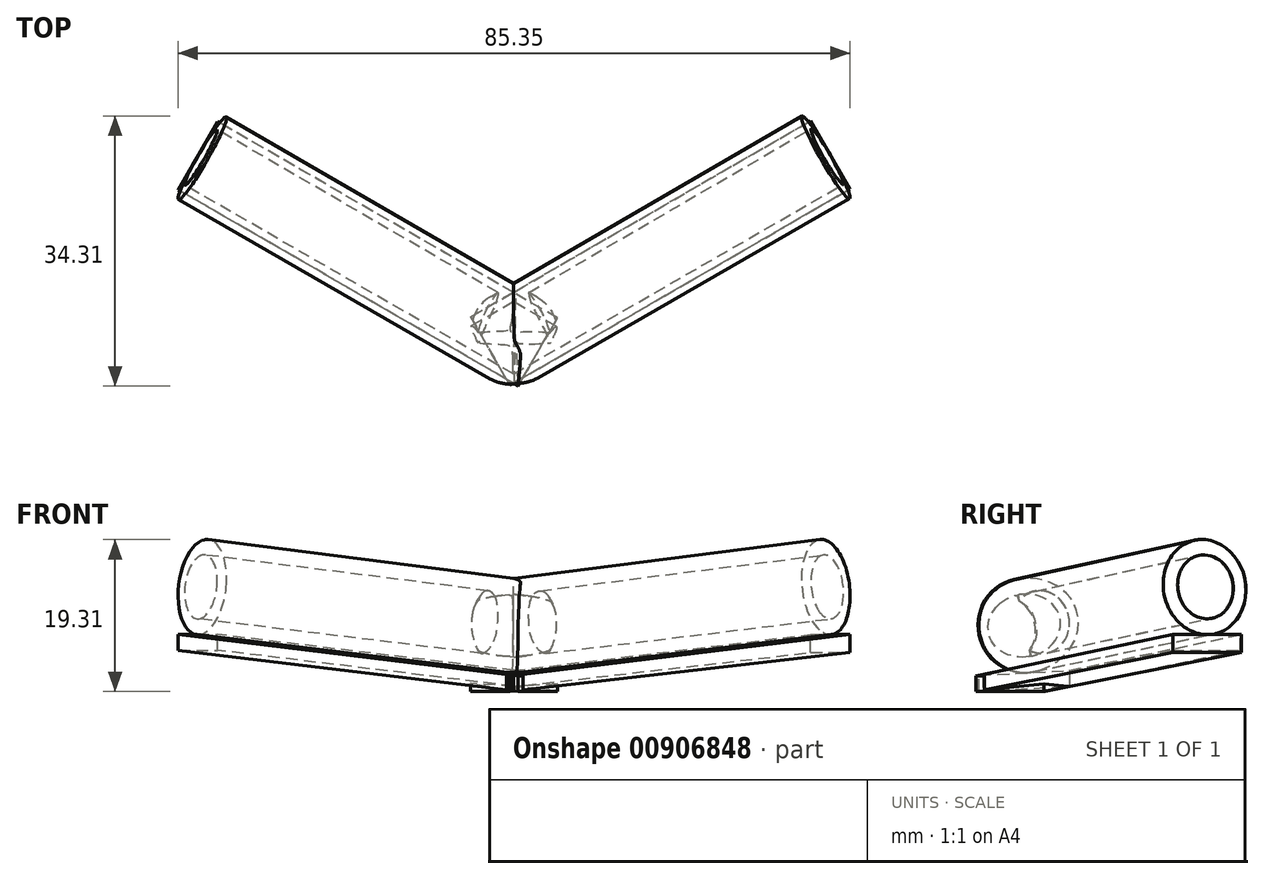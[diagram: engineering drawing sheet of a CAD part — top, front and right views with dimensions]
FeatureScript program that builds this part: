
annotation { "Feature Type Name" : "Feature", "Feature Type Description" : "" }
export const myFeature = defineFeature(function(context is Context, id is Id, definition is map)
    precondition{}
    {
        {
            var Q0;
            Q0=qCreatedBy(makeId("Front.planeOp"),FACE);
            var sketch = newSketch(context, id + "F0", { "sketchPlane" : qUnion([Q0])});
            skLineSegment(sketch, "E0", {"start": v(0, 16.98) * mm, "end": v(0, -4.1) * mm});
            skSolve(sketch);
        }
        {
            var Q0;
            Q0=qCreatedBy(makeId("Right.planeOp"),FACE);
            var Q1;
            Q1=sQuery(id+"F0.wireOp",EDGE,"E0");
            cPlane(context, id + "F1", {"entities" : qUnion([Q0, Q1]), "cplaneType" : CPlaneType.LINE_ANGLE, "offset" : 25 * mm, "angle" : 60 * degree, "width" : 150 * mm, "height" : 150 * mm});
        }
        {
            var Q0;
            Q0=qCreatedBy(id+"F1.planeOp",FACE);
            var sketch = newSketch(context, id + "F2", { "sketchPlane" : qUnion([Q0])});
            skLineSegment(sketch, "E1", {"start": v(3.39, 2) * mm, "end": v(3.39, 4) * mm});
            skLineSegment(sketch, "E2", {"start": v(3.39, 4) * mm, "end": v(3.39, 8) * mm});
            skLineSegment(sketch, "E3", {"start": v(3.39, 0) * mm, "end": v(3.39, 2) * mm});
            skLineSegment(sketch, "E4", {"start": v(0.39, 0) * mm, "end": v(50.25, 0) * mm});
            skLineSegment(sketch, "E5.MirrorCS", {"start": v(3.39, 8) * mm, "end": v(-46.38, 13.33) * mm});
            skLineSegment(sketch, "E6.MirrorCS", {"start": v(-46.48, 10.24) * mm, "end": v(-46.48, 14.24) * mm});
            skLineSegment(sketch, "E7.MirrorCS", {"start": v(3.39, 2) * mm, "end": v(-46.48, 7.24) * mm});
            skLineSegment(sketch, "E8.MirrorCS", {"start": v(3.39, 4) * mm, "end": v(-46.48, 9.24) * mm});
            skLineSegment(sketch, "E9.MirrorCS", {"start": v(-46.48, 3) * mm, "end": v(-46.48, 8.24) * mm});
            skLineSegment(sketch, "E10.MirrorCS", {"start": v(3.39, 0) * mm, "end": v(-46.48, 0) * mm});
            skLineSegment(sketch, "E11.MirrorCS", {"start": v(3.39, 2) * mm, "end": v(-46.48, 2) * mm});
            skLineSegment(sketch, "E12.MirrorCS", {"start": v(-46.48, 0) * mm, "end": v(-46.48, 3) * mm});
            skLineSegment(sketch, "E13.MirrorCS", {"start": v(-46.48, 8.24) * mm, "end": v(-46.48, 10.24) * mm});
            skPoint(sketch, "E14", {"position": v(-17.05, -12.14) * mm});
            skLineSegment(sketch, "E15", {"start": v(3.39, 0) * mm, "end": v(-46.48, 4.95) * mm});
            skSolve(sketch);
        }
        {
            var Q0;
            Q0=makeQuery(id+"F2.imprint","IMPRINT",FACE,{"disambiguationData":[TD([[makeQuery(id+"F2.imprint","IMPRINT",EDGE,{"derivedFrom":sQuery(id+"F2.wireOp",EDGE,"E7.MirrorCS")}),1.0]])]});
            var Q1;
            {var subQ0=sQuery(id+"F2.wireOp",EDGE,"E3");Q1=makeQuery(id+"F2.imprint","IMPRINT",FACE,{"disambiguationData":[TD([[makeQuery(id+"F2.imprint","IMPRINT",EDGE,{"derivedFrom":subQ0}),1.0]])]});}
            extrude(context, id + "F3", {"entities" : qUnion([Q0, Q1]), "depth" : 10 * mm, "offsetDistance" : 25 * mm, "symmetric" : true});
        }
        {
            var Q0;
            {var subQ0=sQuery(id+"F2.wireOp",EDGE,"E8.MirrorCS");Q0=makeQuery(id+"F2.imprint","IMPRINT",FACE,{"disambiguationData":[TD([[makeQuery(id+"F2.imprint","IMPRINT",EDGE,{"derivedFrom":subQ0}),1.0]])]});}
            var Q1;
            {var subQ0=sQuery(id+"F2.wireOp",EDGE,"E7.MirrorCS");Q1=makeQuery(id+"F2.imprint","IMPRINT",FACE,{"disambiguationData":[TD([[makeQuery(id+"F2.imprint","IMPRINT",EDGE,{"derivedFrom":subQ0}),-1.0]])]});}
            var Q2;
            Q2=sQuery(id+"F2.wireOp",EDGE,"E5.MirrorCS");
            revolve(context, id + "F4", {"operationType" : NewBodyOperationType.ADD, "surfaceOperationType" : NewSurfaceOperationType.NEW, "entities" : qUnion([Q0, Q1]), "axis" : qUnion([Q2]), "revolveType" : RevolveType.FULL});
        }
        {
            var Q0;
            Q0=qCreatedBy(makeId("Right.planeOp"),FACE);
            var Q1;
            Q1=sQuery(id+"F0.wireOp",EDGE,"E0");
            cPlane(context, id + "F5", {"entities" : qUnion([Q0, Q1]), "cplaneType" : CPlaneType.LINE_ANGLE, "offset" : 25 * mm, "angle" : 60 * degree, "oppositeDirection" : true, "width" : 150 * mm, "height" : 150 * mm});
        }
        {
            var Q0;
            Q0=qCreatedBy(id+"F5.planeOp",FACE);
            var sketch = newSketch(context, id + "F6", { "sketchPlane" : qUnion([Q0])});
            skLineSegment(sketch, "E16", {"start": v(3.6, 2) * mm, "end": v(3.6, 4) * mm});
            skLineSegment(sketch, "E17", {"start": v(3.6, 4) * mm, "end": v(3.6, 8) * mm});
            skLineSegment(sketch, "E18", {"start": v(3.6, 0) * mm, "end": v(3.6, 2) * mm});
            skLineSegment(sketch, "E19", {"start": v(-0.2, 0) * mm, "end": v(49.67, 0) * mm});
            skLineSegment(sketch, "E20.MirrorCS", {"start": v(3.6, 8) * mm, "end": v(-46.16, 13.33) * mm});
            skLineSegment(sketch, "E21.MirrorCS", {"start": v(-46.25, 10.24) * mm, "end": v(-46.25, 14.24) * mm});
            skLineSegment(sketch, "E22.MirrorCS", {"start": v(3.6, 2) * mm, "end": v(-46.25, 7.24) * mm});
            skLineSegment(sketch, "E23.MirrorCS", {"start": v(3.6, 4) * mm, "end": v(-46.25, 9.24) * mm});
            skLineSegment(sketch, "E24.MirrorCS", {"start": v(-46.25, 3) * mm, "end": v(-46.25, 8.24) * mm});
            skLineSegment(sketch, "E25.MirrorCS", {"start": v(3.6, 0) * mm, "end": v(-46.25, 0) * mm});
            skLineSegment(sketch, "E26.MirrorCS", {"start": v(3.6, 2) * mm, "end": v(-46.25, 2) * mm});
            skLineSegment(sketch, "E27.MirrorCS", {"start": v(-46.25, 0) * mm, "end": v(-46.25, 2) * mm});
            skLineSegment(sketch, "E28.MirrorCS", {"start": v(-46.25, 8.24) * mm, "end": v(-46.25, 10.24) * mm});
            skLineSegment(sketch, "E29", {"start": v(-46.25, 2) * mm, "end": v(-46.25, 3) * mm});
            skLineSegment(sketch, "E30", {"start": v(3.6, 0) * mm, "end": v(-46.25, 5.24) * mm});
            skSolve(sketch);
        }
        {
            var Q0;
            Q0=makeQuery(id+"F6.imprint","IMPRINT",FACE,{"disambiguationData":[TD([[makeQuery(id+"F6.imprint","IMPRINT",EDGE,{"derivedFrom":sQuery(id+"F6.wireOp",EDGE,"E22.MirrorCS")}),1.0]])]});
            var Q1;
            {var subQ0=sQuery(id+"F6.wireOp",EDGE,"E18");Q1=makeQuery(id+"F6.imprint","IMPRINT",FACE,{"disambiguationData":[TD([[makeQuery(id+"F6.imprint","IMPRINT",EDGE,{"derivedFrom":subQ0}),1.0]])]});}
            extrude(context, id + "F7", {"entities" : qUnion([Q0, Q1]), "depth" : 10 * mm, "offsetDistance" : 25 * mm, "symmetric" : true});
        }
        {
            var Q0;
            Q0=makeQuery(id+"F6.imprint","IMPRINT",FACE,{"disambiguationData":[TD([[makeQuery(id+"F6.imprint","IMPRINT",EDGE,{"derivedFrom":sQuery(id+"F6.wireOp",EDGE,"E16")}),1.0]])]});
            var Q1;
            Q1=sQuery(id+"F6.wireOp",EDGE,"E20.MirrorCS");
            revolve(context, id + "F8", {"surfaceOperationType" : NewSurfaceOperationType.NEW, "entities" : qUnion([Q0]), "axis" : qUnion([Q1]), "revolveType" : RevolveType.FULL});
        }
        {
            var Q0;
            Q0=makeQuery(id+"F4.opRevolve","SWEPT_EDGE",EDGE,{"disambiguationData":[OSD([sQuery(id+"F2.wireOp",EDGE,"E1"),sQuery(id+"F2.wireOp",EDGE,"E3"),sQuery(id+"F2.wireOp",EDGE,"E7.MirrorCS"),sQuery(id+"F2.wireOp",EDGE,"E11.MirrorCS")])]});
            var Q1;
            Q1=makeQuery(id+"F8.opRevolve","SWEPT_EDGE",EDGE,{"disambiguationData":[OSD([sQuery(id+"F6.wireOp",EDGE,"E16"),sQuery(id+"F6.wireOp",EDGE,"E18"),sQuery(id+"F6.wireOp",EDGE,"E22.MirrorCS"),sQuery(id+"F6.wireOp",EDGE,"E26.MirrorCS")])]});
            var Q2;
            Q2=makeQuery(id+"FcDGojZFEvCuKsQ_3.opExtrude","CAP_EDGE",EDGE,{"disambiguationData":[OSD([sQuery(id+"F6.wireOp",EDGE,"E18")])],"isStart":false});
            var Q3;
            Q3=makeQuery(id+"F9EvrPw9UCSVND9_1.opExtrude","CAP_EDGE",EDGE,{"disambiguationData":[OSD([sQuery(id+"F2.wireOp",EDGE,"E3")])],"isStart":true});
            fillet(context, id + "F9", {"entities" : qUnion([Q0, Q1, Q2, Q3]), "radius" : 5 * mm, "tangentPropagation" : true, "allowEdgeOverflow" : false});
        }
        {
            var Q0;
            Q0=makeQuery(id+"F3.opExtrude","SWEPT_BODY",BODY,{"disambiguationData":[OSD([sQuery(id+"F2.wireOp",EDGE,"E7.MirrorCS"),sQuery(id+"F2.wireOp",EDGE,"E9.MirrorCS"),sQuery(id+"F2.wireOp",EDGE,"E11.MirrorCS"),sQuery(id+"F2.wireOp",EDGE,"E12.MirrorCS")])]});
            var Q1;
            Q1=makeQuery(id+"F7.opExtrude","SWEPT_BODY",BODY,{"disambiguationData":[OSD([sQuery(id+"F6.wireOp",EDGE,"E22.MirrorCS"),sQuery(id+"F6.wireOp",EDGE,"E24.MirrorCS"),sQuery(id+"F6.wireOp",EDGE,"E26.MirrorCS"),sQuery(id+"F6.wireOp",EDGE,"E29")])]});
            var Q2;
            Q2=makeQuery(id+"FcDGojZFEvCuKsQ_3.opExtrude","SWEPT_BODY",BODY,{"disambiguationData":[OSD([sQuery(id+"F6.wireOp",EDGE,"E18"),sQuery(id+"F6.wireOp",EDGE,"E25.MirrorCS"),sQuery(id+"F6.wireOp",EDGE,"E26.MirrorCS"),sQuery(id+"F6.wireOp",EDGE,"E27.MirrorCS")])]});
            var Q3;
            Q3=makeQuery(id+"F8.opRevolve","SWEPT_BODY",BODY,{"disambiguationData":[OSD([sQuery(id+"F6.wireOp",EDGE,"E16"),sQuery(id+"F6.wireOp",EDGE,"E22.MirrorCS"),sQuery(id+"F6.wireOp",EDGE,"E23.MirrorCS"),sQuery(id+"F6.wireOp",EDGE,"E24.MirrorCS"),sQuery(id+"F6.wireOp",EDGE,"E28.MirrorCS")])]});
            var Q4;
            Q4=makeQuery(id+"F4.opRevolve","SWEPT_BODY",BODY,{"disambiguationData":[OSD([sQuery(id+"F2.wireOp",EDGE,"E1"),sQuery(id+"F2.wireOp",EDGE,"E7.MirrorCS"),sQuery(id+"F2.wireOp",EDGE,"E8.MirrorCS"),sQuery(id+"F2.wireOp",EDGE,"E9.MirrorCS"),sQuery(id+"F2.wireOp",EDGE,"E13.MirrorCS")])]});
            booleanBodies(context, id + "F10", {"operationType" : BooleanOperationType.UNION, "tools" : qUnion([Q0, Q1, Q2, Q3, Q4])});
        }
    });
